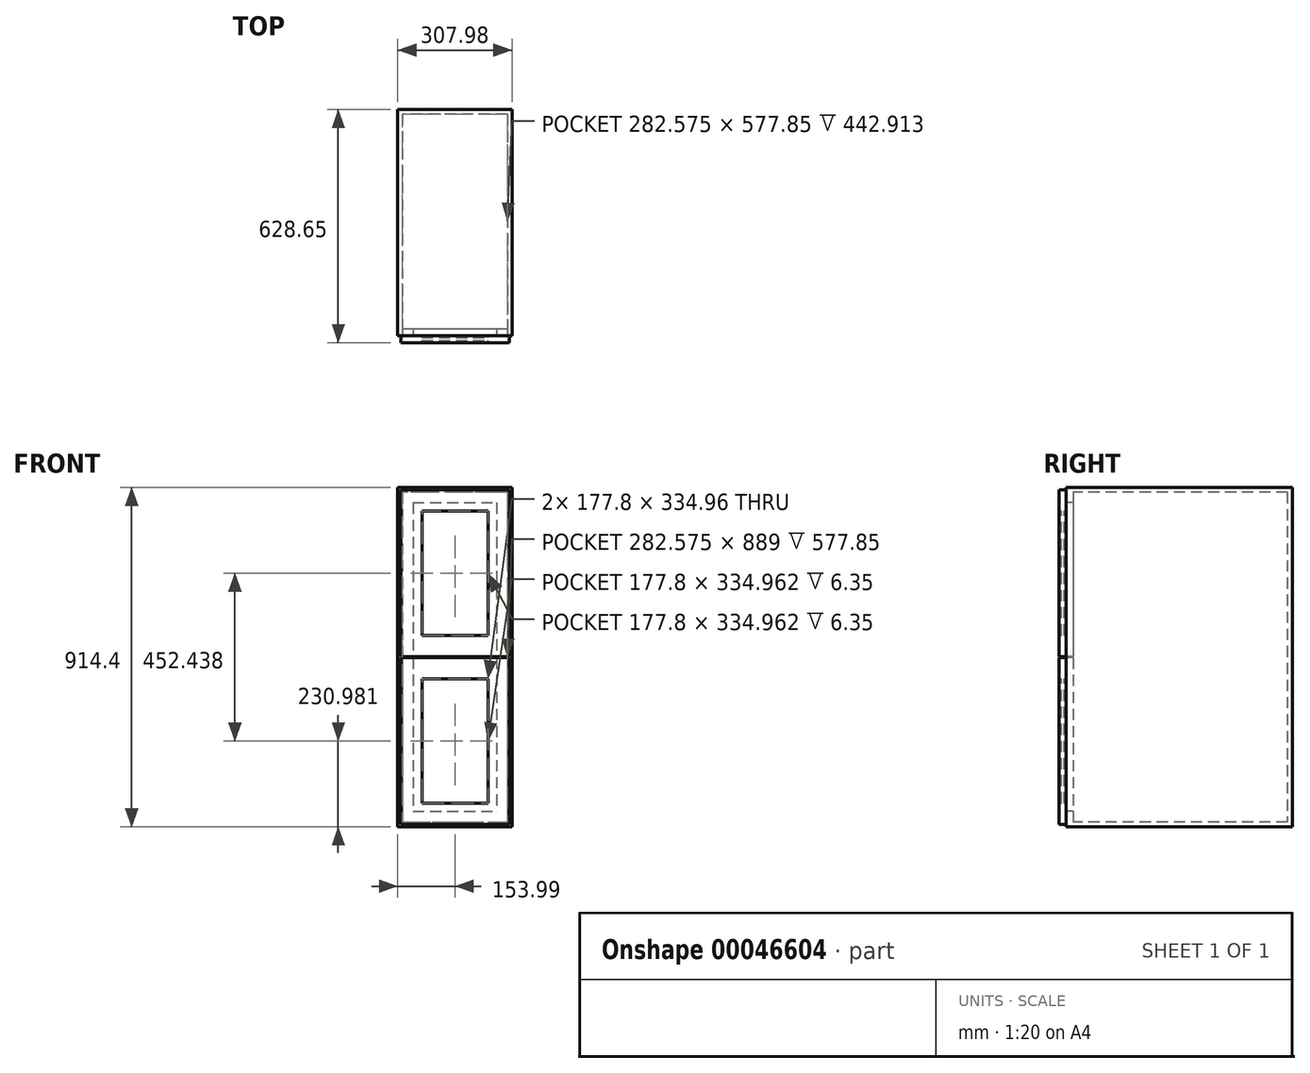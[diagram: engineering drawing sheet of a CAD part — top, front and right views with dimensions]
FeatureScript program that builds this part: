
annotation { "Feature Type Name" : "Feature", "Feature Type Description" : "" }
export const myFeature = defineFeature(function(context is Context, id is Id, definition is map)
    precondition{}
    {
        {
            var Q0;
            Q0=qCreatedBy(makeId("Top.planeOp"),FACE);
            var sketch = newSketch(context, id + "F0", { "sketchPlane" : qUnion([Q0])});
            skLineSegment(sketch, "E0.rect.bottom", {"start": v(153.99, 304.8) * mm, "end": v(-153.99, 304.8) * mm});
            skLineSegment(sketch, "E0.rect.top", {"start": v(153.99, -304.8) * mm, "end": v(-153.99, -304.8) * mm});
            skLineSegment(sketch, "E0.rect.left", {"start": v(153.99, 304.8) * mm, "end": v(153.99, -304.8) * mm});
            skLineSegment(sketch, "E0.rect.right", {"start": v(-153.99, 304.8) * mm, "end": v(-153.99, -304.8) * mm});
            skPoint(sketch, "E0.rect.middle", {"position": v(0, 0) * mm});
            skSolve(sketch);
        }
        {
            var Q0;
            Q0=qSketchRegion(id+"F0",true);
            extrude(context, id + "F1", {"entities" : qUnion([Q0]), "depth" : 914.4 * mm});
        }
        {
            var Q0;
            Q0=makeQuery(id+"F1.opExtrude","SWEPT_FACE",FACE,{"disambiguationData":[OSD([sQuery(id+"F0.wireOp",EDGE,"E0.rect.top")])]});
            shell(context, id + "F2", {"entities" : qUnion([Q0]), "thickness" : 12.7 * mm});
        }
        {
            var Q0;
            Q0=makeQuery(id+"F1.opExtrude","SWEPT_FACE",FACE,{"disambiguationData":[OSD([sQuery(id+"F0.wireOp",EDGE,"E0.rect.top")])]});
            var sketch = newSketch(context, id + "F3", { "sketchPlane" : qUnion([Q0])});
            skLineSegment(sketch, "E1", {"start": v(-153.99, 457.2) * mm, "end": v(153.99, 457.2) * mm, "construction": true});
            skLineSegment(sketch, "E2.rect.bottom", {"start": v(-153.99, 436.56) * mm, "end": v(153.99, 436.56) * mm});
            skLineSegment(sketch, "E2.rect.top", {"start": v(-153.99, 477.84) * mm, "end": v(153.99, 477.84) * mm});
            skLineSegment(sketch, "E2.rect.left", {"start": v(-153.99, 436.56) * mm, "end": v(-153.99, 477.84) * mm});
            skLineSegment(sketch, "E2.rect.right", {"start": v(153.99, 436.56) * mm, "end": v(153.99, 477.84) * mm});
            skPoint(sketch, "E2.rect.middle", {"position": v(0, 457.2) * mm});
            skLineSegment(sketch, "E3.bottom", {"start": v(-146.05, 6.35) * mm, "end": v(146.05, 6.35) * mm});
            skLineSegment(sketch, "E3.top", {"start": v(-146.05, 455.61) * mm, "end": v(146.05, 455.61) * mm});
            skLineSegment(sketch, "E3.left", {"start": v(-146.05, 6.35) * mm, "end": v(-146.05, 455.61) * mm});
            skLineSegment(sketch, "E3.right", {"start": v(146.05, 6.35) * mm, "end": v(146.05, 455.61) * mm});
            skLineSegment(sketch, "E4.rect.bottom", {"start": v(-112.71, 873.13) * mm, "end": v(112.71, 873.13) * mm});
            skLineSegment(sketch, "E4.rect.top", {"start": v(-112.71, 41.28) * mm, "end": v(112.71, 41.28) * mm});
            skLineSegment(sketch, "E4.rect.left", {"start": v(-112.71, 873.13) * mm, "end": v(-112.71, 41.28) * mm});
            skLineSegment(sketch, "E4.rect.right", {"start": v(112.71, 873.13) * mm, "end": v(112.71, 41.28) * mm});
            skLineSegment(sketch, "E5.bottom", {"start": v(-88.9, 63.5) * mm, "end": v(88.9, 63.5) * mm});
            skLineSegment(sketch, "E5.top", {"start": v(-88.9, 398.46) * mm, "end": v(88.9, 398.46) * mm});
            skLineSegment(sketch, "E5.left", {"start": v(-88.9, 63.5) * mm, "end": v(-88.9, 398.46) * mm});
            skLineSegment(sketch, "E5.right", {"start": v(88.9, 63.5) * mm, "end": v(88.9, 398.46) * mm});
            skLineSegment(sketch, "E6.bottom", {"start": v(-146.05, 458.79) * mm, "end": v(146.05, 458.79) * mm});
            skLineSegment(sketch, "E6.top", {"start": v(-146.05, 908.05) * mm, "end": v(146.05, 908.05) * mm});
            skLineSegment(sketch, "E6.left", {"start": v(-146.05, 458.79) * mm, "end": v(-146.05, 908.05) * mm});
            skLineSegment(sketch, "E6.right", {"start": v(146.05, 458.79) * mm, "end": v(146.05, 908.05) * mm});
            skLineSegment(sketch, "E7.bottom", {"start": v(-88.9, 515.94) * mm, "end": v(88.9, 515.94) * mm});
            skLineSegment(sketch, "E7.top", {"start": v(-88.9, 850.9) * mm, "end": v(88.9, 850.9) * mm});
            skLineSegment(sketch, "E7.left", {"start": v(-88.9, 515.94) * mm, "end": v(-88.9, 850.9) * mm});
            skLineSegment(sketch, "E7.right", {"start": v(88.9, 515.94) * mm, "end": v(88.9, 850.9) * mm});
            skSolve(sketch);
        }
        {
            var Q0;
            {var subQ1=sQuery(id+"F3.wireOp",EDGE,"E4.rect.bottom");Q0=makeQuery(id+"F3.imprint","IMPRINT",FACE,{"disambiguationData":[TD([[makeQuery(id+"F3.imprint","IMPRINT",EDGE,{"derivedFrom":subQ1}),1.0]])]});}
            var Q1;
            {var subQ0=sQuery(id+"F0.wireOp",EDGE,"E0.rect.top");var subQ1=makeQuery(id+"F1.opExtrude","CAP_EDGE",EDGE,{"disambiguationData":[OSD([subQ0])],"isStart":false});Q1=makeQuery(id+"F3.imprint","IMPRINT",FACE,{"disambiguationData":[TD([[makeQuery(id+"F3.imprint","IMPRINT",EDGE,{"derivedFrom":subQ1}),1.0]])]});}
            var Q2;
            {var subQ0=sQuery(id+"F3.wireOp",EDGE,"E4.rect.top");Q2=makeQuery(id+"F3.imprint","IMPRINT",FACE,{"disambiguationData":[TD([[makeQuery(id+"F3.imprint","IMPRINT",EDGE,{"derivedFrom":subQ0}),-1.0]])]});}
            var Q3;
            {var subQ1=sQuery(id+"F3.wireOp",EDGE,"E3.bottom");Q3=makeQuery(id+"F3.imprint","IMPRINT",FACE,{"disambiguationData":[TD([[makeQuery(id+"F3.imprint","IMPRINT",EDGE,{"derivedFrom":subQ1}),-1.0]])]});}
            var Q4;
            {var subQ0=sQuery(id+"F3.wireOp",EDGE,"E3.bottom");Q4=makeQuery(id+"F3.imprint","IMPRINT",FACE,{"disambiguationData":[TD([[makeQuery(id+"F3.imprint","IMPRINT",EDGE,{"derivedFrom":subQ0}),1.0]])]});}
            var Q5;
            {var subQ0=sQuery(id+"F3.wireOp",EDGE,"E4.rect.left");var subQ1=sQuery(id+"F3.wireOp",EDGE,"E2.rect.bottom");var subQ2=makeQuery(id+"F3.imprint","INTERSECT",VERTEX,{"derivedFrom":[subQ1,subQ0]});Q5=makeQuery(id+"F3.imprint","IMPRINT",FACE,{"disambiguationData":[TD([[makeQuery(id+"F3.imprint","IMPRINT",EDGE,{"disambiguationData":[TD([[subQ2,1.0]])],"derivedFrom":subQ0}),-1.0]])]});}
            var Q6;
            {var subQ0=sQuery(id+"F3.wireOp",EDGE,"E2.rect.left");Q6=makeQuery(id+"F3.imprint","IMPRINT",FACE,{"disambiguationData":[TD([[makeQuery(id+"F3.imprint","IMPRINT",EDGE,{"derivedFrom":subQ0}),1.0]])]});}
            var Q7;
            {var subQ0=sQuery(id+"F3.wireOp",EDGE,"E3.left");var subQ5=sQuery(id+"F3.wireOp",EDGE,"E3.top");var subQ6=makeQuery(id+"F3.imprint","INTERSECT",VERTEX,{"derivedFrom":[subQ5,subQ0]});Q7=makeQuery(id+"F3.imprint","IMPRINT",FACE,{"disambiguationData":[TD([[makeQuery(id+"F3.imprint","IMPRINT",EDGE,{"disambiguationData":[TD([[subQ6,1.0]])],"derivedFrom":subQ0}),-1.0]])]});}
            var Q8;
            {var subQ0=sQuery(id+"F3.wireOp",EDGE,"E4.rect.left");var subQ1=sQuery(id+"F3.wireOp",EDGE,"E2.rect.top");var subQ2=makeQuery(id+"F3.imprint","INTERSECT",VERTEX,{"derivedFrom":[subQ1,subQ0]});Q8=makeQuery(id+"F3.imprint","IMPRINT",FACE,{"disambiguationData":[TD([[makeQuery(id+"F3.imprint","IMPRINT",EDGE,{"disambiguationData":[TD([[subQ2,-1.0]])],"derivedFrom":subQ0}),-1.0]])]});}
            var Q9;
            {var subQ0=sQuery(id+"F3.wireOp",EDGE,"E4.rect.right");var subQ1=sQuery(id+"F3.wireOp",EDGE,"E2.rect.top");var subQ2=makeQuery(id+"F3.imprint","INTERSECT",VERTEX,{"derivedFrom":[subQ1,subQ0]});Q9=makeQuery(id+"F3.imprint","IMPRINT",FACE,{"disambiguationData":[TD([[makeQuery(id+"F3.imprint","IMPRINT",EDGE,{"disambiguationData":[TD([[subQ2,-1.0]])],"derivedFrom":subQ0}),1.0]])]});}
            var Q10;
            {var subQ0=sQuery(id+"F3.wireOp",EDGE,"E4.rect.right");var subQ1=sQuery(id+"F3.wireOp",EDGE,"E2.rect.bottom");var subQ2=makeQuery(id+"F3.imprint","INTERSECT",VERTEX,{"derivedFrom":[subQ1,subQ0]});Q10=makeQuery(id+"F3.imprint","IMPRINT",FACE,{"disambiguationData":[TD([[makeQuery(id+"F3.imprint","IMPRINT",EDGE,{"disambiguationData":[TD([[subQ2,1.0]])],"derivedFrom":subQ0}),1.0]])]});}
            var Q11;
            {var subQ7=sQuery(id+"F3.wireOp",EDGE,"E2.rect.right");Q11=makeQuery(id+"F3.imprint","IMPRINT",FACE,{"disambiguationData":[TD([[makeQuery(id+"F3.imprint","IMPRINT",EDGE,{"derivedFrom":subQ7}),-1.0]])]});}
            var Q12;
            {var subQ0=sQuery(id+"F3.wireOp",EDGE,"E3.right");var subQ5=sQuery(id+"F3.wireOp",EDGE,"E3.top");var subQ6=makeQuery(id+"F3.imprint","INTERSECT",VERTEX,{"derivedFrom":[subQ5,subQ0]});Q12=makeQuery(id+"F3.imprint","IMPRINT",FACE,{"disambiguationData":[TD([[makeQuery(id+"F3.imprint","IMPRINT",EDGE,{"disambiguationData":[TD([[subQ6,1.0]])],"derivedFrom":subQ0}),1.0]])]});}
            extrude(context, id + "F4", {"entities" : qUnion([Q0, Q1, Q2, Q3, Q4, Q5, Q6, Q7, Q8, Q9, Q10, Q11, Q12]), "operationType" : NewBodyOperationType.ADD, "oppositeDirection" : true, "depth" : 19.05 * mm});
        }
        {
            var Q0;
            {var subQ0=sQuery(id+"F3.wireOp",EDGE,"E4.rect.top");Q0=makeQuery(id+"F3.imprint","IMPRINT",FACE,{"disambiguationData":[TD([[makeQuery(id+"F3.imprint","IMPRINT",EDGE,{"derivedFrom":subQ0}),-1.0]])]});}
            var Q1;
            {var subQ0=sQuery(id+"F3.wireOp",EDGE,"E3.bottom");Q1=makeQuery(id+"F3.imprint","IMPRINT",FACE,{"disambiguationData":[TD([[makeQuery(id+"F3.imprint","IMPRINT",EDGE,{"derivedFrom":subQ0}),1.0]])]});}
            var Q2;
            {var subQ1=sQuery(id+"F3.wireOp",EDGE,"E4.rect.top");Q2=makeQuery(id+"F3.imprint","IMPRINT",FACE,{"disambiguationData":[TD([[makeQuery(id+"F3.imprint","IMPRINT",EDGE,{"derivedFrom":subQ1}),1.0]])]});}
            var Q3;
            {var subQ0=sQuery(id+"F3.wireOp",EDGE,"E4.rect.left");var subQ1=sQuery(id+"F3.wireOp",EDGE,"E2.rect.bottom");var subQ2=makeQuery(id+"F3.imprint","INTERSECT",VERTEX,{"derivedFrom":[subQ1,subQ0]});Q3=makeQuery(id+"F3.imprint","IMPRINT",FACE,{"disambiguationData":[TD([[makeQuery(id+"F3.imprint","IMPRINT",EDGE,{"disambiguationData":[TD([[subQ2,-1.0]])],"derivedFrom":subQ1}),1.0]])]});}
            var Q4;
            {var subQ0=sQuery(id+"F3.wireOp",EDGE,"E4.rect.left");var subQ1=sQuery(id+"F3.wireOp",EDGE,"E2.rect.bottom");var subQ2=makeQuery(id+"F3.imprint","INTERSECT",VERTEX,{"derivedFrom":[subQ1,subQ0]});Q4=makeQuery(id+"F3.imprint","IMPRINT",FACE,{"disambiguationData":[TD([[makeQuery(id+"F3.imprint","IMPRINT",EDGE,{"disambiguationData":[TD([[subQ2,1.0]])],"derivedFrom":subQ0}),-1.0]])]});}
            var Q5;
            {var subQ0=sQuery(id+"F3.wireOp",EDGE,"E4.rect.right");var subQ1=sQuery(id+"F3.wireOp",EDGE,"E2.rect.bottom");var subQ2=makeQuery(id+"F3.imprint","INTERSECT",VERTEX,{"derivedFrom":[subQ1,subQ0]});Q5=makeQuery(id+"F3.imprint","IMPRINT",FACE,{"disambiguationData":[TD([[makeQuery(id+"F3.imprint","IMPRINT",EDGE,{"disambiguationData":[TD([[subQ2,1.0]])],"derivedFrom":subQ0}),1.0]])]});}
            var Q6;
            {var subQ0=sQuery(id+"F3.wireOp",EDGE,"E3.right");var subQ5=sQuery(id+"F3.wireOp",EDGE,"E3.top");var subQ6=makeQuery(id+"F3.imprint","INTERSECT",VERTEX,{"derivedFrom":[subQ5,subQ0]});Q6=makeQuery(id+"F3.imprint","IMPRINT",FACE,{"disambiguationData":[TD([[makeQuery(id+"F3.imprint","IMPRINT",EDGE,{"disambiguationData":[TD([[subQ6,1.0]])],"derivedFrom":subQ0}),1.0]])]});}
            var Q7;
            {var subQ0=sQuery(id+"F3.wireOp",EDGE,"E3.left");var subQ5=sQuery(id+"F3.wireOp",EDGE,"E3.top");var subQ6=makeQuery(id+"F3.imprint","INTERSECT",VERTEX,{"derivedFrom":[subQ5,subQ0]});Q7=makeQuery(id+"F3.imprint","IMPRINT",FACE,{"disambiguationData":[TD([[makeQuery(id+"F3.imprint","IMPRINT",EDGE,{"disambiguationData":[TD([[subQ6,1.0]])],"derivedFrom":subQ0}),-1.0]])]});}
            var Q8;
            {var subQ0=sQuery(id+"F3.wireOp",EDGE,"E4.rect.bottom");Q8=makeQuery(id+"F3.imprint","IMPRINT",FACE,{"disambiguationData":[TD([[makeQuery(id+"F3.imprint","IMPRINT",EDGE,{"derivedFrom":subQ0}),1.0]])]});}
            var Q9;
            {var subQ1=sQuery(id+"F3.wireOp",EDGE,"E4.rect.bottom");Q9=makeQuery(id+"F3.imprint","IMPRINT",FACE,{"disambiguationData":[TD([[makeQuery(id+"F3.imprint","IMPRINT",EDGE,{"derivedFrom":subQ1}),-1.0]])]});}
            var Q10;
            {var subQ0=sQuery(id+"F3.wireOp",EDGE,"E4.rect.left");var subQ1=sQuery(id+"F3.wireOp",EDGE,"E2.rect.top");var subQ2=makeQuery(id+"F3.imprint","INTERSECT",VERTEX,{"derivedFrom":[subQ1,subQ0]});Q10=makeQuery(id+"F3.imprint","IMPRINT",FACE,{"disambiguationData":[TD([[makeQuery(id+"F3.imprint","IMPRINT",EDGE,{"disambiguationData":[TD([[subQ2,-1.0]])],"derivedFrom":subQ0}),-1.0]])]});}
            var Q11;
            {var subQ0=sQuery(id+"F3.wireOp",EDGE,"E4.rect.left");var subQ1=sQuery(id+"F3.wireOp",EDGE,"E2.rect.top");var subQ2=makeQuery(id+"F3.imprint","INTERSECT",VERTEX,{"derivedFrom":[subQ1,subQ0]});Q11=makeQuery(id+"F3.imprint","IMPRINT",FACE,{"disambiguationData":[TD([[makeQuery(id+"F3.imprint","IMPRINT",EDGE,{"disambiguationData":[TD([[subQ2,-1.0]])],"derivedFrom":subQ1}),-1.0]])]});}
            var Q12;
            {var subQ0=sQuery(id+"F3.wireOp",EDGE,"E4.rect.right");var subQ1=sQuery(id+"F3.wireOp",EDGE,"E2.rect.top");var subQ2=makeQuery(id+"F3.imprint","INTERSECT",VERTEX,{"derivedFrom":[subQ1,subQ0]});Q12=makeQuery(id+"F3.imprint","IMPRINT",FACE,{"disambiguationData":[TD([[makeQuery(id+"F3.imprint","IMPRINT",EDGE,{"disambiguationData":[TD([[subQ2,-1.0]])],"derivedFrom":subQ0}),1.0]])]});}
            var Q13;
            {var subQ0=sQuery(id+"F3.wireOp",EDGE,"E6.right");var subQ5=sQuery(id+"F3.wireOp",EDGE,"E6.bottom");var subQ6=makeQuery(id+"F3.imprint","INTERSECT",VERTEX,{"derivedFrom":[subQ5,subQ0]});Q13=makeQuery(id+"F3.imprint","IMPRINT",FACE,{"disambiguationData":[TD([[makeQuery(id+"F3.imprint","IMPRINT",EDGE,{"disambiguationData":[TD([[subQ6,-1.0]])],"derivedFrom":subQ0}),1.0]])]});}
            var Q14;
            {var subQ1=sQuery(id+"F3.wireOp",EDGE,"E6.top");Q14=makeQuery(id+"F3.imprint","IMPRINT",FACE,{"disambiguationData":[TD([[makeQuery(id+"F3.imprint","IMPRINT",EDGE,{"derivedFrom":subQ1}),-1.0]])]});}
            var Q15;
            {var subQ0=sQuery(id+"F3.wireOp",EDGE,"E6.left");var subQ5=sQuery(id+"F3.wireOp",EDGE,"E6.bottom");var subQ6=makeQuery(id+"F3.imprint","INTERSECT",VERTEX,{"derivedFrom":[subQ5,subQ0]});Q15=makeQuery(id+"F3.imprint","IMPRINT",FACE,{"disambiguationData":[TD([[makeQuery(id+"F3.imprint","IMPRINT",EDGE,{"disambiguationData":[TD([[subQ6,-1.0]])],"derivedFrom":subQ0}),-1.0]])]});}
            extrude(context, id + "F5", {"entities" : qUnion([Q0, Q1, Q2, Q3, Q4, Q5, Q6, Q7, Q8, Q9, Q10, Q11, Q12, Q13, Q14, Q15]), "operationType" : NewBodyOperationType.ADD, "depth" : 19.05 * mm});
        }
        {
            var Q0;
            Q0=makeQuery(id+"F5.opExtrude","SWEPT_FACE",FACE,{"disambiguationData":[OSD([sQuery(id+"F3.wireOp",EDGE,"E5.right")])]});
            var sketch = newSketch(context, id + "F6", { "sketchPlane" : qUnion([Q0])});
            skLineSegment(sketch, "E8.bottom", {"start": v(309.56, 63.5) * mm, "end": v(317.5, 63.5) * mm});
            skLineSegment(sketch, "E8.top", {"start": v(309.56, 398.46) * mm, "end": v(317.5, 398.46) * mm});
            skLineSegment(sketch, "E8.left", {"start": v(309.56, 63.5) * mm, "end": v(309.56, 398.46) * mm});
            skLineSegment(sketch, "E8.right", {"start": v(317.5, 63.5) * mm, "end": v(317.5, 398.46) * mm});
            skLineSegment(sketch, "E9.bottom", {"start": v(309.56, 515.94) * mm, "end": v(317.5, 515.94) * mm});
            skLineSegment(sketch, "E9.top", {"start": v(309.56, 850.9) * mm, "end": v(317.5, 850.9) * mm});
            skLineSegment(sketch, "E9.left", {"start": v(309.56, 515.94) * mm, "end": v(309.56, 850.9) * mm});
            skLineSegment(sketch, "E9.right", {"start": v(317.5, 515.94) * mm, "end": v(317.5, 850.9) * mm});
            skSolve(sketch);
        }
        {
            var Q0;
            Q0=qSketchRegion(id+"F6",true);
            extrude(context, id + "F7", {"entities" : qUnion([Q0]), "operationType" : NewBodyOperationType.ADD, "endBound" : BoundingType.UP_TO_NEXT, "depth" : 25.4 * mm});
        }
    });
